# Revit family: Lighting_Floor-Mounted_Pholc_Apollo_Floor
name_source: partatom
category: Lighting Fixtures
revit_build: Autodesk Revit 2017 (Build: 20190508_0315(x64)
units: mm (PartAtom-declared; Revit-internal decimal feet)

## family parameters
Always vertical = Yes
Cut with Voids When Loaded = No
Light Source = Yes
OmniClass Number = 23.80.70.00
OmniClass Title = Lighting
Part Type = Normal
Room Calculation Point = No
Round Connector Dimension = Use Diameter
Shared = No
Work Plane-Based = No

## types (2) — shared parameters
AssetType = Movable
BIMObjectName = Lighting_Floor-Mounted_Pholc_Apollo_Floor
Brand = Pholc
Category = Floor
Collection = Apollo
Color Filter = 16777215
ConvergoRefNr = 0103-1912-0001-SE
Description = With a composition that alludes to mass and weight, Apollo is a lamp made from a solid piece of machine-turned brass or aluminium. Its conical shapes balance end-on-end like spinning gyros, emphasising a dynamic, downward, thrusting force. A lamp with a real heightened material presence, with its surfaces left deliberately raw. The Apollo family comes in a range of colours that can be used singularly or hanging in various heights as a group constellation. A new addition to the family is the distinctive Apollo 180 floor lamp, in lacquered or black anodised aluminium. The upward turning conical shapes give an indirect light.
Designer = Broberg & Ridderstrale
Dimming Lamp Color Temperature Shift = <None>
DurationUnit = Hours
Emit Shape Visible in Rendering = No
Emit from Circle Diameter = 18 mm  [stored 0.0590551 ft]
HasProtectiveEarth = No
IP_Code = IP 20
IfcExportAs = IfcLightFixtureType
IfcExportType = NOTDEFINED
InsulationStandardClass = Class II
Light Source Symbol Length = 3048 mm  [stored 10 ft]
LightFixtureMountingType = FreeStanding
LightFixturePlacingType = Floor
Manufacturer = Pholc
ManufacturerName = Pholc
ManufacturerURL = https://www.pholc.se
Material = Aluminium & PVC
NBSDescription = General purpose luminaires
NBSReference = 90-60-50/405
Name = Pholc_Apollo_Floor
NominalCurrent = 0 A
NominalDepth = 250 mm
NominalFrequencyRange = 0 Hz
NominalHeight = 1800 mm  [stored 5.90551 ft]
NominalVoltage = 230 V
NominalVoltageCalc = 0 V
NominalWidth = 250 mm
NumberOfPoles = 1
PhaseAngle = 0.00°
ProductInformation = With a composition that alludes to mass and weight, Apollo is a lamp made from a solid piece of machine-turned brass or aluminium.
Shape = Sculptured
Size = 250x250x1800 mm
Spot Beam Angle = 30.00°
Spot Field Angle = 90.00°
Tilt Angle = 90.00°
TotalWattage = 7 W
URL = https://www.pholc.se
Uniclass2 = Pr_70_70_48_32
Uniclass2015Description = Free standing luminaires
Uniclass2015Reference = Pr_70_70_48_32
UsageCurrent = 0 A
Version = 1
VersionDate = 21/04/2020
WarrantyDurationUnit = Years
zero-valued in all types: DefaultElevation, ElectricalDeviceNominalPower, MaintenanceFactor, NominalDiameter, NominalRadius, NumberOfSources

## per-type parameters (varying)
| type | ArticleNumber | Color | LightFixtureMainMaterial | LightFixtureSecondaryMaterial | ModelReference |
| Apollo 180 Floor - Black Magic | 792415 | Black | Black Anodized Aluminum | Black ink | 792415 |
| Apollo 180 Floor - Aluminium | 792414 | Grey | Aluminum | Aluminum | 792414 |

note: column(s) folded — value = type name in every type: Model

note: [stored X ft] marks values corroborated as IEEE doubles in the binary element streams (Revit-internal decimal feet)

## geometry (parser evidence)
native form markers: Sweep x6
no freeform markers — native parametric forms only
